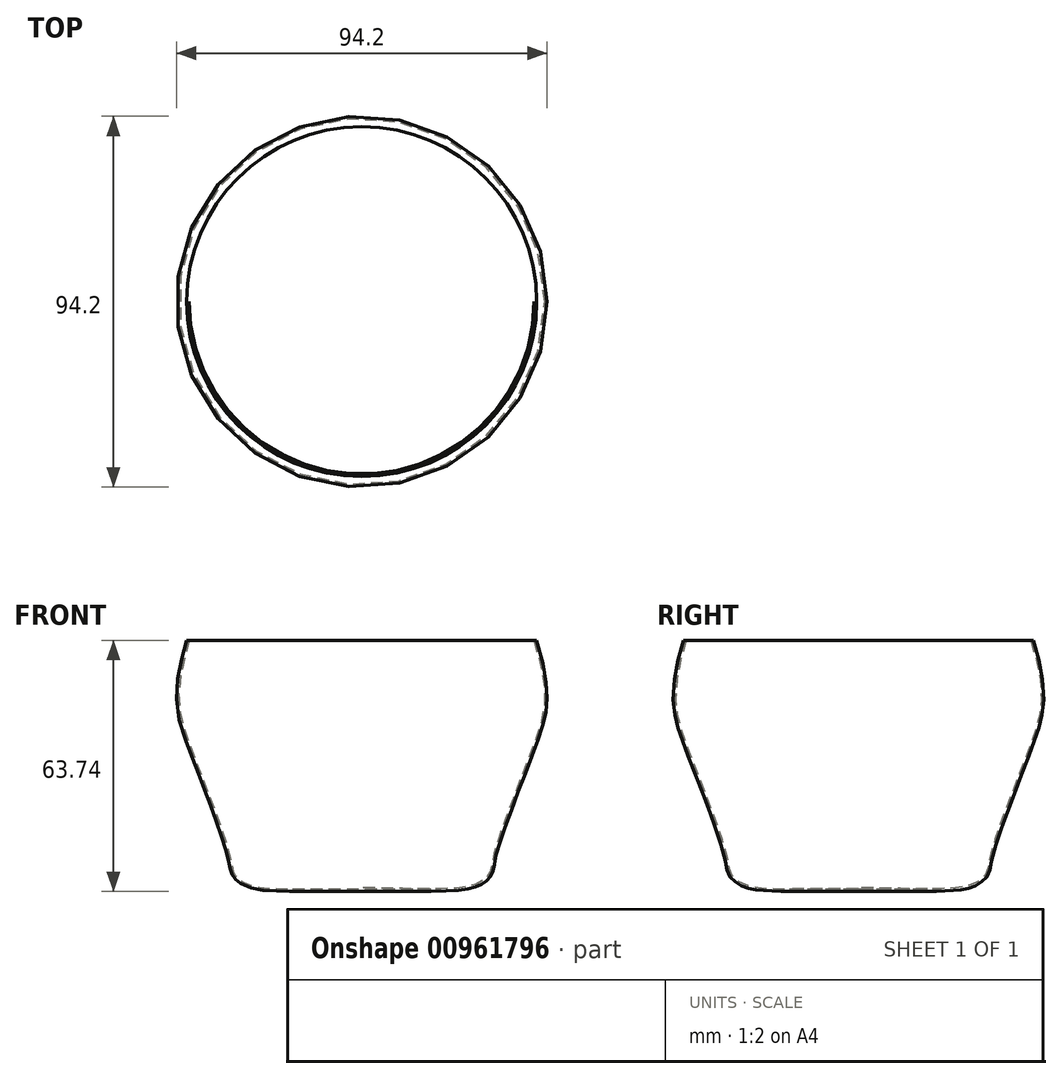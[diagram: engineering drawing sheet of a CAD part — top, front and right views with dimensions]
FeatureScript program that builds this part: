
annotation { "Feature Type Name" : "Feature", "Feature Type Description" : "" }
export const myFeature = defineFeature(function(context is Context, id is Id, definition is map)
    precondition{}
    {
        {
            var Q0;
            Q0=qCreatedBy(makeId("Front.planeOp"),FACE);
            var sketch = newSketch(context, id + "F0", { "sketchPlane" : qUnion([Q0])});
            skLineSegment(sketch, "E0", {"start": v(0, 0) * mm, "end": v(0, 63.5) * mm});
            skLineSegment(sketch, "E1", {"start": v(0, 63.5) * mm, "end": v(44.45, 63.5) * mm});
            skFitSpline(sketch, "E2", {"points": [v(44.45, 63.5) * mm, v(44.45, 37.32) * mm, v(34.25, 9.31) * mm, v(32.9, 3.86) * mm, v(30.39, 1.58) * mm, v(24.62, 0) * mm, v(0, 0) * mm], "startDerivative": vector(52.62, -175.84) * mm, "endDerivative": vector(-111.87, 0) * mm});
            skSolve(sketch);
        }
        {
            var Q0;
            Q0=makeQuery(id+"F0.imprint","IMPRINT",FACE,{"disambiguationData":[TD([[makeQuery(id+"F0.imprint","IMPRINT",EDGE,{"derivedFrom":sQuery(id+"F0.wireOp",EDGE,"E0")}),-1.0]])]});
            var Q1;
            Q1=sQuery(id+"F0.wireOp",EDGE,"E2");
            var Q2;
            Q2=sQuery(id+"F0.wireOp",EDGE,"E0");
            revolve(context, id + "F1", {"surfaceOperationType" : NewSurfaceOperationType.NEW, "entities" : qUnion([Q0]), "surfaceEntities" : qUnion([Q1]), "axis" : qUnion([Q2]), "revolveType" : RevolveType.FULL});
        }
        {
            var Q0;
            Q0=makeQuery(id+"F1.opRevolve","SWEPT_FACE",FACE,{"disambiguationData":[OSD([sQuery(id+"F0.wireOp",EDGE,"E1")])]});
            shell(context, id + "F2", {"entities" : qUnion([Q0]), "thickness" : 0.6 * mm});
        }
    });
